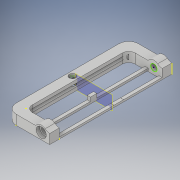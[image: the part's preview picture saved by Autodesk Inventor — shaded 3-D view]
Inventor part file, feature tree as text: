
AUTODESK INVENTOR PART (.ipt)
format: ipt  version: 2018 (Build 220112000, 112)  size: 569,856 bytes
history: native  units: in
note: dims shown in document units (in); Inventor stores cm internally (conversion verified against a paired STEP export)
features: sketch x39, extrude x25, fillet x7, hole x2, plane x1, mirror x1
ambient origin geometry x8: Origin, YZ Plane, XZ Plane, XY Plane, X Axis, Y Axis, Z Axis, Center Point
bodies: Solid1 (feature_tree)
feature tree (75):
  extrude  "Extrusion1"  Depth=0.375in
  sketch  "Sketch2"  dims[d3=0.375in d4=0.5in d5=0.375in d6=0.0in]
  extrude  "Extrusion2"  Depth=0.5in
  fillet  "Fillet1"  Radius=0.375in
  extrude  "Extrusion3"  Depth=0.375in
  extrude  "Extrusion4"  Depth=0.25in
  plane  "Work Plane1"
  mirror  "Mirror1"
  fillet  "Fillet2"  Radius=0.24in
  extrude  "Extrusion5"  Depth=0.375in
  sketch  "Sketch6"  dims[d17=1.0in d18=0.0in d19=0.24in d20=0.0in]
  extrude  "Extrusion6"  Depth=0.24in TaperAngle=0.0deg
  extrude  "Extrusion7"  Depth=0.375in
  fillet  "Fillet3"  Radius=0.25in
  fillet  "Fillet4"  Radius=0.375in
  fillet  "Fillet5"  Radius=0.25in
  fillet  "Fillet6"  Radius=0.125in
  sketch  "Sketch9"  dims[d30=0.125in d31=0.125in]
  extrude  "Extrusion8"  Depth=0.035in
  sketch  "Sketch11"  dims[d35=0.2in]
  sketch  "Sketch12"  dims[d36=0.2in d37=0.75in d38=0.375in d39=0.25in d40=0.5635in d41=0.35in d42=0.0in]
  hole  "Hole1"  [1 undecoded]
  hole  "Hole2"  [1 undecoded]
  sketch  "Sketch14"  dims[d51=3.5in d52=0.375in d53=0.0in]
  extrude  "Extrusion9"  Depth=0.125in
  sketch  "Sketch16"  dims[d58=0.4375in d59=0.0in d60=0.0625in d61=0.0in]
  extrude  "Extrusion10"  Depth=0.375in TaperAngle=0.0deg
  extrude  "Extrusion11"  Depth=0.25in
  extrude  "Extrusion12"  Depth=0.0625in TaperAngle=0.0deg
  sketch  "Sketch20"  dims[d72=0.39in d73=0.135in d74=0.0in]
  sketch  "Sketch21"  dims[d75=0.39in d76=0.135in d77=0.0in]
  sketch  "Sketch22"  dims[d78=0.4475in d79=0.0in d80=0.375in d81=0.0in]
  extrude  "Extrusion13"  Depth=0.125in
  extrude  "Extrusion14"  Depth=0.25in TaperAngle=0.0deg
  fillet  "Fillet7"  Radius=0.25in
  extrude  "Extrusion15"  Depth=0.125in
  extrude  "Extrusion16"  Depth=0.135in TaperAngle=0.0deg
  extrude  "Extrusion17"  Depth=0.135in TaperAngle=0.0deg
  extrude  "Extrusion18"  Depth=0.375in TaperAngle=0.0deg
  sketch  "Sketch29"  dims[d100=0.15in d101=0.0in]
  extrude  "Extrusion19"  Depth=0.375in TaperAngle=0.0deg
  sketch  "Sketch31"
  extrude  "Extrusion20"  Depth=0.375in TaperAngle=0.0deg
  extrude  "Extrusion21"  Depth=0.125in
  sketch  "Sketch34"
  sketch  "Sketch35"
  extrude  "Extrusion22"  Depth=0.375in TaperAngle=0.0deg
  extrude  "Extrusion23"  Depth=0.0425in TaperAngle=0.0deg
  extrude  "Extrusion24"  Depth=0.25in
  extrude  "Extrusion25"  [1 undecoded]
  sketch  "Sketch1"  dims[d0=1.3in d1=0.375in]
  sketch  "Sketch3"  dims[d7=0.375in d8=0.0in d9=0.375in]
  sketch  "Sketch4"  dims[d10=0.24in d11=0.0in d12=0.25in d13=0.24in d14=0.0in]
  sketch  "Sketch5"  dims[d15=2.0in d16=0.375in]
  sketch  "Sketch7"  dims[d21=0.375in d22=0.0in d23=0.375in d24=0.25in d25=0.375in d26=0.25in d27=0.125in]
  sketch  "Sketch8"  dims[d28=0.035in d29=0.035in]
  sketch  "Sketch10"  dims[d32=4.375in d33=0.0in d34=0.2in]
  sketch  "Sketch13"  dims[d43=0.2in d44=0.75in d45=0.375in d46=0.25in d47=0.5635in d48=0.35in d49=0.0in d50=0.125in]
  sketch  "Sketch15"  dims[d56=0.25in d57=0.25in]
  sketch  "Sketch17"  dims[d62=0.04in d63=0.0in d64=0.125in]
  sketch  "Sketch18"  dims[d65=0.075in d66=4.04in d67=0.0in d68=0.25in]
  sketch  "Sketch19"  dims[d69=0.075in d70=0.0in d71=0.125in]
  sketch  "Sketch23"  dims[d82=0.25in d83=0.375in d84=0.0in]
  sketch  "Sketch24"  dims[d85=0.125in d86=0.375in d87=0.0in]
  sketch  "Sketch25"  dims[d88=0.125in d89=0.0in d90=0.125in]
  sketch  "Sketch26"  dims[d91=0.15in d92=0.375in d93=0.0in]
  sketch  "Sketch27"  dims[d94=0.148in d95=0.0in d96=0.0425in d97=0.0in]
  sketch  "Sketch28"  dims[d98=0.125in d99=0.25in]
  sketch  "Sketch30"
  sketch  "Sketch32"
  sketch  "Sketch33"
  sketch  "Sketch36"
  sketch  "Sketch37"
  sketch  "Sketch38"
  sketch  "Sketch39"
note: 3 required parameter values undecoded (feature->parameter linkage not recoverable at this tier; creation-order binding heuristic only, values carry confidence <= 0.55)
